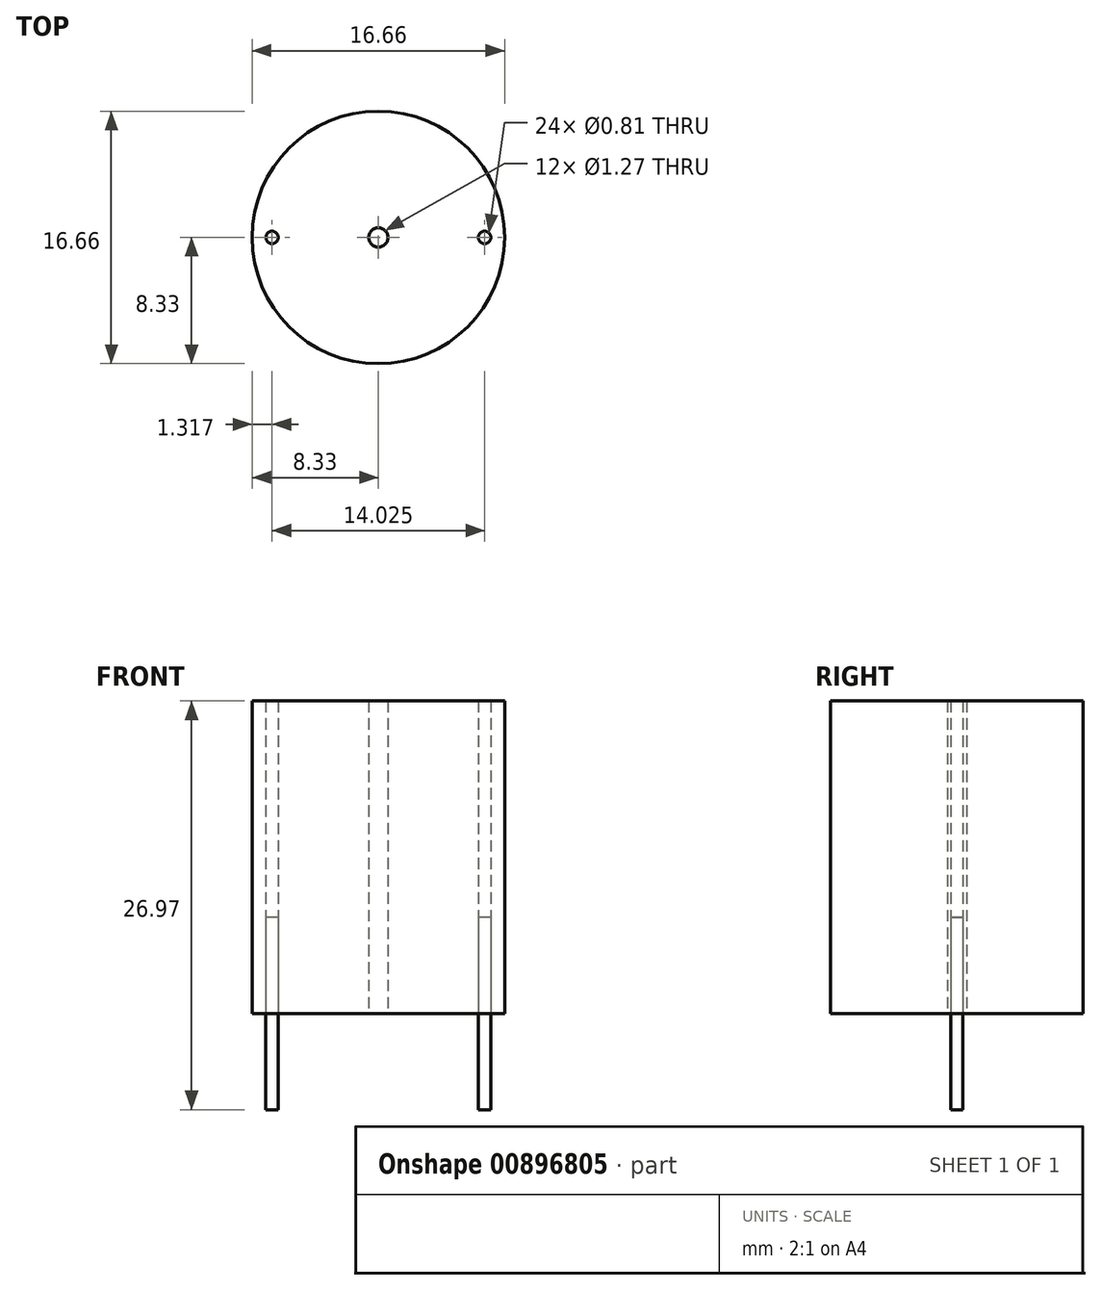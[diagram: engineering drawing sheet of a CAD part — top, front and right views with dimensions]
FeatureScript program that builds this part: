
annotation { "Feature Type Name" : "Feature", "Feature Type Description" : "" }
export const myFeature = defineFeature(function(context is Context, id is Id, definition is map)
    precondition{}
    {
        {
            var Q0;
            Q0=qCreatedBy(makeId("Top.planeOp"),FACE);
            var sketch = newSketch(context, id + "F0", { "sketchPlane" : qUnion([Q0])});
            skCircle(sketch, "E0", {"center": v(0, 0) * mm, "radius": 8.33 * mm});
            skCircle(sketch, "E1", {"center": v(0, 0) * mm, "radius": 0.64 * mm});
            skLineSegment(sketch, "E2", {"start": v(8.23, 1.27) * mm, "end": v(5.7, 1.27) * mm});
            skLineSegment(sketch, "E3", {"start": v(5.7, 1.27) * mm, "end": v(5.7, -1.27) * mm});
            skLineSegment(sketch, "E4", {"start": v(5.7, -1.27) * mm, "end": v(8.23, -1.27) * mm});
            skLineSegment(sketch, "E5", {"start": v(-8.23, 1.27) * mm, "end": v(-5.7, 1.27) * mm});
            skLineSegment(sketch, "E6", {"start": v(-5.7, 1.27) * mm, "end": v(-5.7, -1.27) * mm});
            skLineSegment(sketch, "E7", {"start": v(-5.7, -1.27) * mm, "end": v(-8.23, -1.27) * mm});
            skCircle(sketch, "E8", {"center": v(-7.01, 0) * mm, "radius": 0.4 * mm});
            skCircle(sketch, "E9", {"center": v(7.01, 0) * mm, "radius": 0.4 * mm});
            skSolve(sketch);
        }
        {
            var Q0;
            Q0=makeQuery(id+"F0.imprint","IMPRINT",FACE,{"disambiguationData":[TD([[makeQuery(id+"F0.imprint","IMPRINT",EDGE,{"derivedFrom":sQuery(id+"F0.wireOp",EDGE,"E0")}),1.0]])]});
            var Q1;
            {var subQ1=sQuery(id+"F0.wireOp",EDGE,"E5");Q1=makeQuery(id+"F0.imprint","IMPRINT",FACE,{"disambiguationData":[TD([[makeQuery(id+"F0.imprint","IMPRINT",EDGE,{"derivedFrom":subQ1}),-1.0]])]});}
            var Q2;
            {var subQ1=sQuery(id+"F0.wireOp",EDGE,"E2");Q2=makeQuery(id+"F0.imprint","IMPRINT",FACE,{"disambiguationData":[TD([[makeQuery(id+"F0.imprint","IMPRINT",EDGE,{"derivedFrom":subQ1}),1.0]])]});}
            extrude(context, id + "F1", {"entities" : qUnion([Q0, Q1, Q2]), "depth" : 20.62 * mm, "offsetDistance" : 25.4 * mm});
        }
        {
            var Q0;
            Q0=makeQuery(id+"F0.imprint","IMPRINT",FACE,{"disambiguationData":[TD([[makeQuery(id+"F0.imprint","IMPRINT",EDGE,{"derivedFrom":sQuery(id+"F0.wireOp",EDGE,"E8")}),1.0]])]});
            var Q1;
            Q1=makeQuery(id+"F0.imprint","IMPRINT",FACE,{"disambiguationData":[TD([[makeQuery(id+"F0.imprint","IMPRINT",EDGE,{"derivedFrom":sQuery(id+"F0.wireOp",EDGE,"E9")}),1.0]])]});
            extrude(context, id + "F2", {"entities" : qUnion([Q0, Q1]), "depth" : 6.35 * mm, "offsetDistance" : 25.4 * mm, "hasSecondDirection" : true, "secondDirectionOppositeDirection" : true, "secondDirectionDepth" : 6.35 * mm});
        }
    });
